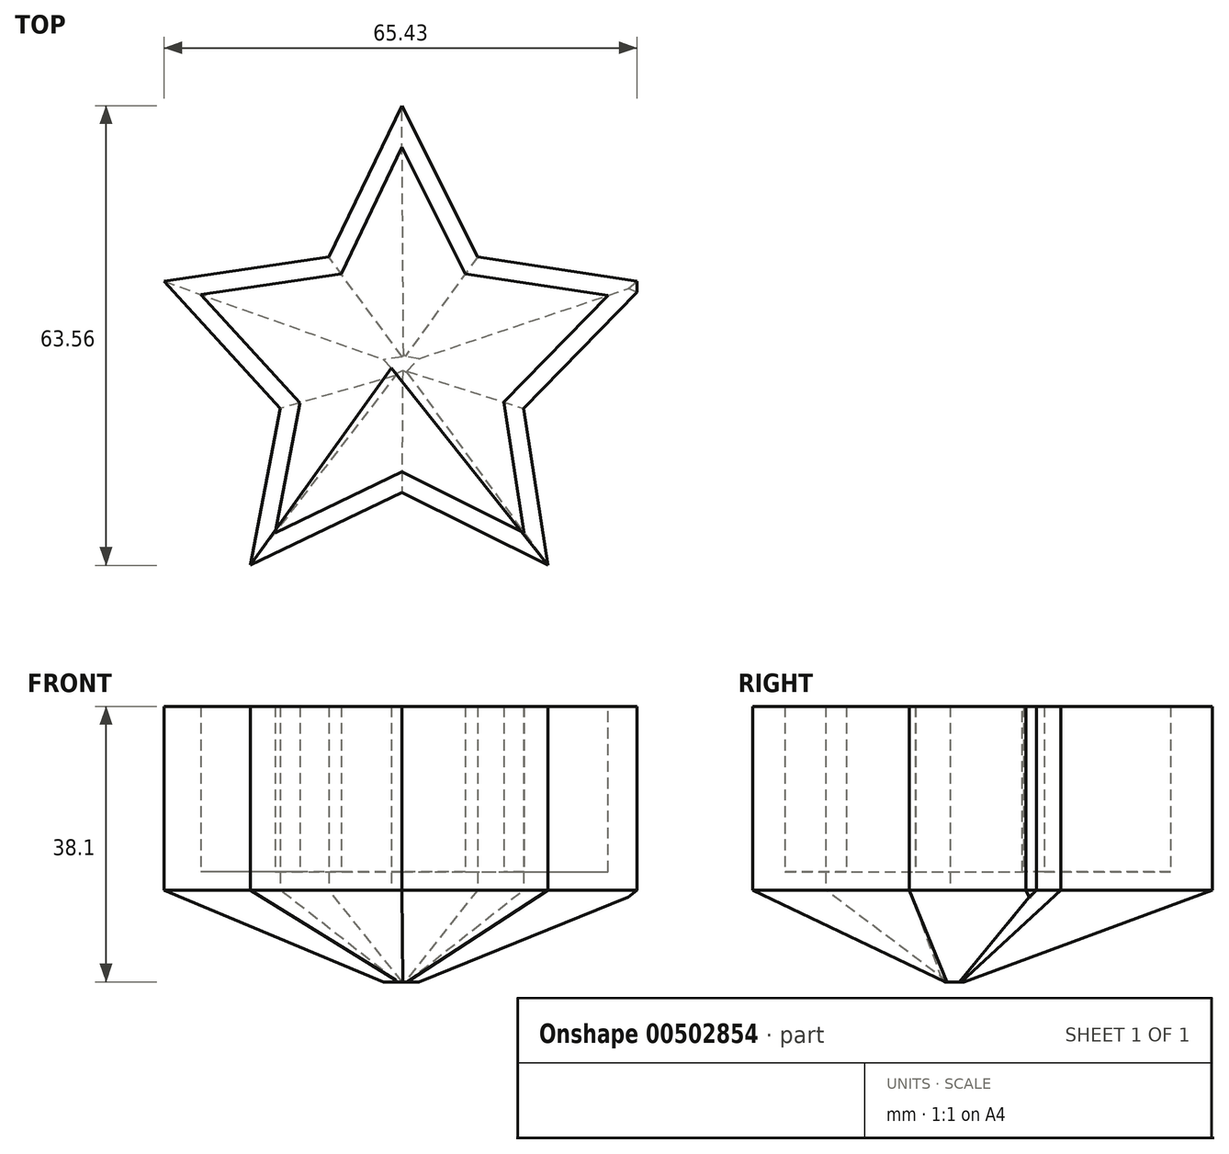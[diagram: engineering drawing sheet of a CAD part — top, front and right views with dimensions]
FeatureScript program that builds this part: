
annotation { "Feature Type Name" : "Feature", "Feature Type Description" : "" }
export const myFeature = defineFeature(function(context is Context, id is Id, definition is map)
    precondition{}
    {
        {
            var Q0;
            Q0=qCreatedBy(makeId("Top.planeOp"),FACE);
            var sketch = newSketch(context, id + "F0", { "sketchPlane" : qUnion([Q0])});
            skLineSegment(sketch, "E0", {"start": v(1.45, 38.08) * mm, "end": v(-8.64, 17.14) * mm});
            skLineSegment(sketch, "E1", {"start": v(-8.64, 17.14) * mm, "end": v(-31.45, 13.78) * mm});
            skLineSegment(sketch, "E2", {"start": v(-19.48, -25.48) * mm, "end": v(-15.37, -3.8) * mm});
            skLineSegment(sketch, "E3", {"start": v(-15.37, -3.8) * mm, "end": v(-31.45, 13.78) * mm});
            skLineSegment(sketch, "E4", {"start": v(-19.48, -25.48) * mm, "end": v(1.45, -15.38) * mm});
            skLineSegment(sketch, "E5", {"start": v(1.45, -15.38) * mm, "end": v(21.64, -25.48) * mm});
            skLineSegment(sketch, "E6", {"start": v(21.64, -25.48) * mm, "end": v(18.28, -3.8) * mm});
            skLineSegment(sketch, "E7", {"start": v(18.28, -3.8) * mm, "end": v(33.98, 12.28) * mm});
            skLineSegment(sketch, "E8", {"start": v(11.92, 17.14) * mm, "end": v(33.98, 13.78) * mm});
            skLineSegment(sketch, "E9", {"start": v(33.98, 13.78) * mm, "end": v(33.98, 12.28) * mm});
            skLineSegment(sketch, "E10", {"start": v(11.92, 17.14) * mm, "end": v(1.45, 38.08) * mm});
            skLineSegment(sketch, "E11", {"start": v(0, 1.81) * mm, "end": v(11.92, 17.14) * mm});
            skLineSegment(sketch, "E12", {"start": v(0, 1.81) * mm, "end": v(33.98, 12.28) * mm});
            skLineSegment(sketch, "E13", {"start": v(0, 1.81) * mm, "end": v(16.03, -3.8) * mm});
            skLineSegment(sketch, "E14", {"start": v(16.03, -3.8) * mm, "end": v(18.28, -3.8) * mm});
            skLineSegment(sketch, "E15", {"start": v(0, 1.81) * mm, "end": v(21.64, -25.48) * mm});
            skLineSegment(sketch, "E16", {"start": v(0, 1.81) * mm, "end": v(-19.48, -25.48) * mm});
            skLineSegment(sketch, "E17", {"start": v(0, 1.81) * mm, "end": v(-29.93, 12.28) * mm});
            skLineSegment(sketch, "E18", {"start": v(-29.93, 12.28) * mm, "end": v(0, 1.81) * mm});
            skLineSegment(sketch, "E19", {"start": v(1.45, 3.68) * mm, "end": v(-8.64, 17.14) * mm});
            skLineSegment(sketch, "E20", {"start": v(-0.84, 2.1) * mm, "end": v(-15.37, -2.37) * mm});
            skLineSegment(sketch, "E21", {"start": v(-15.37, -2.37) * mm, "end": v(0, 1.81) * mm});
            skSolve(sketch);
        }
        {
            var Q0;
            Q0=makeQuery(id+"F0.imprint","IMPRINT",FACE,{"disambiguationData":[TD([[makeQuery(id+"F0.imprint","IMPRINT",EDGE,{"derivedFrom":sQuery(id+"F0.wireOp",EDGE,"E4")}),1.0]])]});
            var sketch = newSketch(context, id + "F1", { "sketchPlane" : qUnion([Q0])});
            skSolve(sketch);
        }
        {
            var Q0;
            Q0=qCreatedBy(makeId("Top.planeOp"),FACE);
            var sketch = newSketch(context, id + "F2", { "sketchPlane" : qUnion([Q0])});
            skSolve(sketch);
        }
        {
            var Q0;
            Q0 = qSketchRegion(id + "F2", true);
            var Q1;
            Q1=makeQuery(id+"F0.imprint","IMPRINT",FACE,{"disambiguationData":[TD([[makeQuery(id+"F0.imprint","IMPRINT",EDGE,{"derivedFrom":sQuery(id+"F0.wireOp",EDGE,"E4")}),1.0]])]});
            var Q2;
            Q2=makeQuery(id+"F0.imprint","IMPRINT",FACE,{"disambiguationData":[TD([[makeQuery(id+"F0.imprint","IMPRINT",EDGE,{"derivedFrom":sQuery(id+"F0.wireOp",EDGE,"E0")}),1.0]])]});
            var Q3;
            Q3=makeQuery(id+"F0.imprint","IMPRINT",FACE,{"disambiguationData":[TD([[makeQuery(id+"F0.imprint","IMPRINT",EDGE,{"derivedFrom":sQuery(id+"F0.wireOp",EDGE,"E6")}),1.0]])]});
            var Q4;
            Q4=makeQuery(id+"F0.imprint","IMPRINT",FACE,{"disambiguationData":[TD([[makeQuery(id+"F0.imprint","IMPRINT",EDGE,{"derivedFrom":sQuery(id+"F0.wireOp",EDGE,"E7")}),1.0]])]});
            var Q5;
            {var subQ1=sQuery(id+"F0.wireOp",EDGE,"E8");Q5=makeQuery(id+"F0.imprint","IMPRINT",FACE,{"disambiguationData":[TD([[makeQuery(id+"F0.imprint","IMPRINT",EDGE,{"derivedFrom":subQ1}),-1.0]])]});}
            var Q6;
            Q6=makeQuery(id+"F0.imprint","IMPRINT",FACE,{"disambiguationData":[TD([[makeQuery(id+"F0.imprint","IMPRINT",EDGE,{"derivedFrom":sQuery(id+"F0.wireOp",EDGE,"E1")}),1.0]])]});
            var Q7;
            Q7=makeQuery(id+"F1.imprint","IMPRINT",FACE,{"disambiguationData":[TD([[makeQuery(id+"F1.imprint","IMPRINT",EDGE,{"derivedFrom":makeQuery(id+"F0.imprint","IMPRINT",EDGE,{"derivedFrom":sQuery(id+"F0.wireOp",EDGE,"E4")})}),1.0]])]});
            var Q8;
            {var subQ2=sQuery(id+"F0.wireOp",EDGE,"E20");Q8=makeQuery(id+"F0.imprint","IMPRINT",FACE,{"disambiguationData":[TD([[makeQuery(id+"F0.imprint","IMPRINT",EDGE,{"derivedFrom":subQ2}),1.0]])]});}
            extrude(context, id + "F3", {"entities" : qUnion([Q0, Q1, Q2, Q3, Q4, Q5, Q6, Q7, Q8]), "depth" : 25.4 * mm});
        }
        {
            var Q0;
            Q0=makeQuery(id+"F3.opExtrude","CAP_FACE",FACE,{"disambiguationData":[OSD([sQuery(id+"F0.wireOp",EDGE,"E0"),sQuery(id+"F0.wireOp",EDGE,"E1"),sQuery(id+"F0.wireOp",EDGE,"E2"),sQuery(id+"F0.wireOp",EDGE,"E3"),sQuery(id+"F0.wireOp",EDGE,"E4"),sQuery(id+"F0.wireOp",EDGE,"E5"),sQuery(id+"F0.wireOp",EDGE,"E6"),sQuery(id+"F0.wireOp",EDGE,"E7"),sQuery(id+"F0.wireOp",EDGE,"E8"),sQuery(id+"F0.wireOp",EDGE,"E9"),sQuery(id+"F0.wireOp",EDGE,"E10")])],"isStart":false});
            shell(context, id + "F4", {"entities" : qUnion([Q0]), "thickness" : 2.54 * mm});
        }
        {
            var Q0;
            Q0=makeQuery(id+"F3.opExtrude","CAP_FACE",FACE,{"disambiguationData":[OSD([sQuery(id+"F0.wireOp",EDGE,"E0"),sQuery(id+"F0.wireOp",EDGE,"E1"),sQuery(id+"F0.wireOp",EDGE,"E2"),sQuery(id+"F0.wireOp",EDGE,"E3"),sQuery(id+"F0.wireOp",EDGE,"E4"),sQuery(id+"F0.wireOp",EDGE,"E5"),sQuery(id+"F0.wireOp",EDGE,"E6"),sQuery(id+"F0.wireOp",EDGE,"E7"),sQuery(id+"F0.wireOp",EDGE,"E8"),sQuery(id+"F0.wireOp",EDGE,"E9"),sQuery(id+"F0.wireOp",EDGE,"E10")])],"isStart":true});
            extrude(context, id + "F5", {"entities" : qUnion([Q0]), "depth" : 12.7 * mm, "hasDraft" : true, "draftAngle" : 50 * degree, "draftPullDirection" : true});
        }
    });
